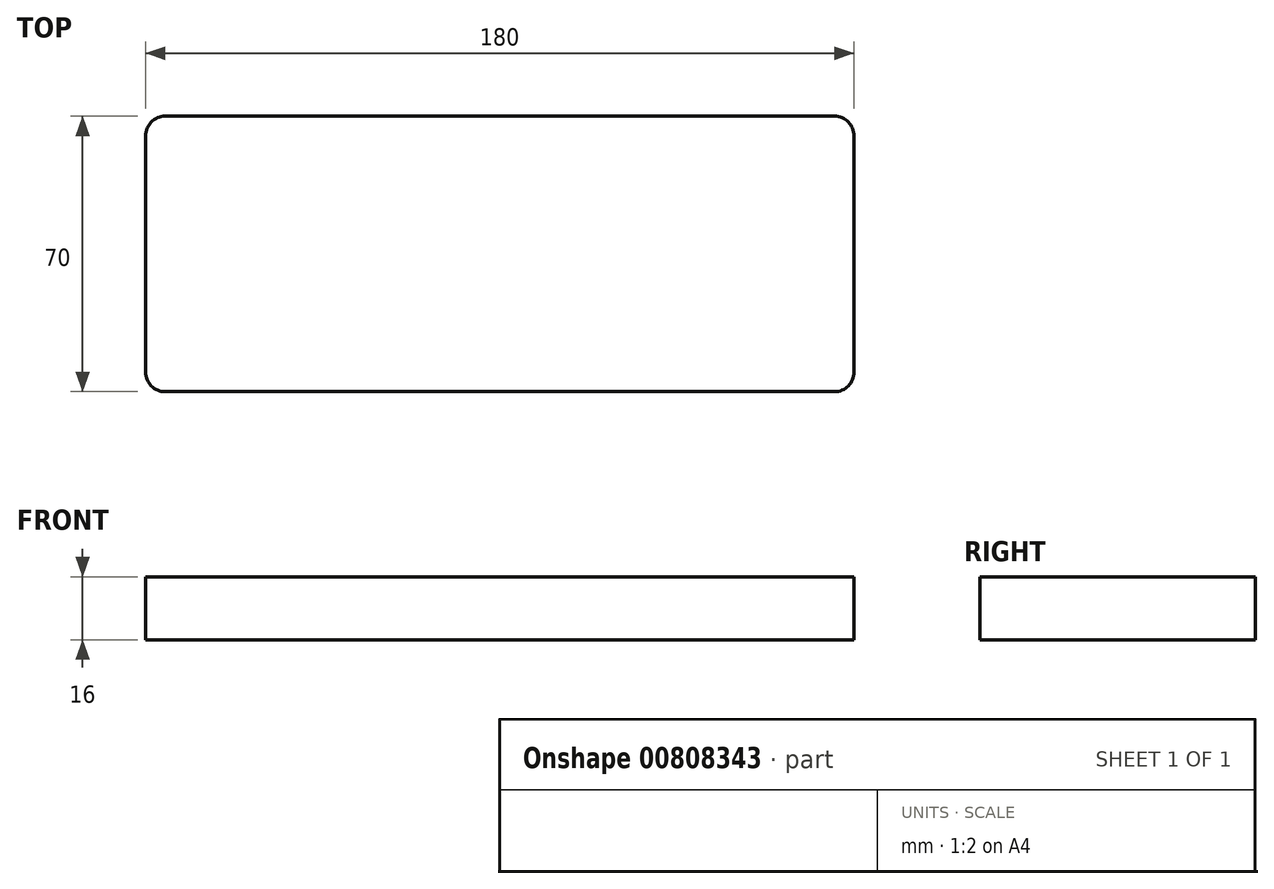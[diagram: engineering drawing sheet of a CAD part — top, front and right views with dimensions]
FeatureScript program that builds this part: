
annotation { "Feature Type Name" : "Feature", "Feature Type Description" : "" }
export const myFeature = defineFeature(function(context is Context, id is Id, definition is map)
    precondition{}
    {
        {
            var Q0;
            Q0=qCreatedBy(makeId("Top.planeOp"),FACE);
            var sketch = newSketch(context, id + "F0", { "sketchPlane" : qUnion([Q0])});
            skLineSegment(sketch, "E0.bottom", {"start": v(0, 0) * mm, "end": v(180, 0) * mm});
            skLineSegment(sketch, "E0.top", {"start": v(0, 70) * mm, "end": v(180, 70) * mm});
            skLineSegment(sketch, "E0.left", {"start": v(0, 0) * mm, "end": v(0, 70) * mm});
            skLineSegment(sketch, "E0.right", {"start": v(180, 0) * mm, "end": v(180, 70) * mm});
            skSolve(sketch);
        }
        {
            var Q0;
            Q0=makeQuery(id+"F0.imprint","IMPRINT",FACE,{"disambiguationData":[TD([[makeQuery(id+"F0.imprint","IMPRINT",EDGE,{"derivedFrom":sQuery(id+"F0.wireOp",EDGE,"E0.bottom")}),1.0]])]});
            extrude(context, id + "F1", {"entities" : qUnion([Q0]), "depth" : 2 * 8 * mm, "offsetDistance" : 25 * mm});
        }
        {
            var Q0;
            Q0=makeQuery(id+"F1.opExtrude","SWEPT_EDGE",EDGE,{"disambiguationData":[OSD([sQuery(id+"F0.wireOp",EDGE,"E0.bottom"),sQuery(id+"F0.wireOp",EDGE,"E0.left")])]});
            var Q1;
            Q1=makeQuery(id+"F1.opExtrude","SWEPT_EDGE",EDGE,{"disambiguationData":[OSD([sQuery(id+"F0.wireOp",EDGE,"E0.top"),sQuery(id+"F0.wireOp",EDGE,"E0.left")])]});
            var Q2;
            Q2=makeQuery(id+"F1.opExtrude","SWEPT_EDGE",EDGE,{"disambiguationData":[OSD([sQuery(id+"F0.wireOp",EDGE,"E0.top"),sQuery(id+"F0.wireOp",EDGE,"E0.right")])]});
            var Q3;
            Q3=makeQuery(id+"F1.opExtrude","SWEPT_EDGE",EDGE,{"disambiguationData":[OSD([sQuery(id+"F0.wireOp",EDGE,"E0.bottom"),sQuery(id+"F0.wireOp",EDGE,"E0.right")])]});
            fillet(context, id + "F2", {"entities" : qUnion([Q0, Q1, Q2, Q3]), "radius" : 5 * mm, "tangentPropagation" : true, "allowEdgeOverflow" : false});
        }
    });
